# Revit family: Drain_Floor_7_Inch_Diameter_Top_Medium-Duty_Zurn-Z507
name_source: partatom
category: Plumbing Fixtures
units: mm (PartAtom-declared; Revit-internal decimal feet)

## family parameters
Always vertical = Yes
Cut with Voids When Loaded = No
Maintain Annotation Orientation = No
OmniClass Number = 23.70.50.21.24.14
OmniClass Title = Deck Waste Water Drains
Part Type = Normal
Room Calculation Point = No
Round Connector Dimension = Use Radius
Shared = No
Work Plane-Based = No

## types (20) — shared parameters
Default Elevation = 0' - 0"
Description = 7 Inch Diameter Top Medium-Duty Drain
Frame only height = 0' - 2 1/4"
Grate Radius = 0' - 3 3/16"
HW Connection = No
Main Material = Iron - Zurn - Cast - Painted - Blue
Manufacturer = Zurn Water, LLC
Manufacurer Brand = Zurn
Model = Z507
Product Documentation Link = https://files.zurn.com
Product Page URL = https://www.zurn.com
Product data url = https://bimobject.com
Trap Primer Radius = 0' - 0 1/4"
URL = www.zurn.com
Veneer Frame = Bronze - Zurn  - Polished Nickel
Vent Connection = No

## per-type parameters (varying)
| type | Approx. Weight (Lbs) | Assembly Code | CW Connection | E Body Height | Flange Height | Frame | Grate | Outlet Radius | Outllet Outer Radius | Type Comments |
| Z507-4IC Outlet | 27 |  | Yes | 0' - 3 3/4" | 0' - 1 15/16" | No | Iron - Zurn - Cast - Painted - Blue | 0' - 2" | 0' - 2 27/32" | Z507-4IC Outlet w/ Optional-P Trap Primer Connection |
| ZN507-4IC Outlet | 27 |  | No | 0' - 3 3/4" | 0' - 2 1/8" | Yes | Bronze - Zurn  - Polished Nickel | 0' - 2" | 0' - 2 27/32" | ZN507-4IC Outlet w/ Optional-P Trap Primer Connection |
| Z507-3IP Outlet | 27 |  | Yes | 0' - 2 3/4" | 0' - 1 15/16" | No | Iron - Zurn - Cast - Painted - Blue | 0' - 1 1/2" | 0' - 2 1/4" | Z507-3IP Outlet w/ Optional-P Trap Primer Connection |
| Z507-4IP Outlet | 27 |  | No | 0' - 2 3/4" | 0' - 1 15/16" | No | Iron - Zurn - Cast - Painted - Blue | 0' - 2" | 0' - 2 13/16" | Z507-4IP Outlet w/ Optional-P Trap Primer Connection |
| Z507-2NH Outlet | 27 | D2030300 | Yes | 0' - 4 3/4" | 0' - 1 15/16" | No | Iron - Zurn - Cast - Painted - Blue | 0' - 1" | 0' - 1 7/32" | Z507-2NH Outlet w/ Optional-P Trap Primer Connection |
| Z507-3NH Outlet | 27 |  | Yes | 0' - 4 3/4" | 0' - 1 15/16" | No | Iron - Zurn - Cast - Painted - Blue | 0' - 1 1/2" | 0' - 1 23/32" | Z507-3NH Outlet w/ Optional-P Trap Primer Connection |
| Z507-4NH Outlet | 27 |  | No | 0' - 4 3/4" | 0' - 1 15/16" | No | Iron - Zurn - Cast - Painted - Blue | 0' - 2" | 0' - 2 7/32" | Z507-4NH Outlet w/ Optional-P Trap Primer Connection |
| Z507-6NH Outlet | 29 |  | No | 0' - 5 1/4" | 0' - 1 15/16" | No | Iron - Zurn - Cast - Painted - Blue | 0' - 3" | 0' - 3 3/16" | Z507-6NH Outlet w/ Optional-P Trap Primer Connection |
| Z507-2NL Outlet | 27 |  | Yes | 0' - 3 9/16" | 0' - 1 15/16" | No | Iron - Zurn - Cast - Painted - Blue | 0' - 1" | 0' - 1 11/16" | Z507-2NL Outlet w/ Optional-P Trap Primer Connection |
| Z507-3NL Outlet | 27 |  | Yes | 0' - 3 9/16" | 0' - 1 15/16" | No | Iron - Zurn - Cast - Painted - Blue | 0' - 1 1/2" | 0' - 2 7/32" | Z507-3NL Outlet w/ Optional-P Trap Primer Connection |
| Z507-4NL Outlet | 27 |  | Yes | 0' - 3 9/16" | 0' - 1 15/16" | No | Iron - Zurn - Cast - Painted - Blue | 0' - 2" | 0' - 2 27/32" | Z507-3NL Outlet w/ Optional-P Trap Primer Connection |
| ZN507-3IP Outlet | 27 | D2030300 | Yes | 0' - 2 3/4" | 0' - 2 1/8" | Yes | Bronze - Zurn  - Polished Nickel | 0' - 1 1/2" | 0' - 2 1/4" | ZN507-3IP Outlet w/ Optional-P Trap Primer Connection |
| ZN507-4IP Outlet | 27 |  | No | 0' - 2 3/4" | 0' - 2 1/8" | Yes | Bronze - Zurn  - Polished Nickel | 0' - 2" | 0' - 2 13/16" | ZN507-4IP Outlet w/ Optional-P Trap Primer Connection |
| ZN507-2NH Outlet | 27 |  | No | 0' - 4 3/4" | 0' - 2 1/8" | Yes | Bronze - Zurn  - Polished Nickel | 0' - 1" | 0' - 1 7/32" | ZN507-2NH Outlet w/ Optional-P Trap Primer Connection |
| ZN507-3NH Outlet | 27 |  | No | 0' - 4 3/4" | 0' - 2 1/8" | Yes | Bronze - Zurn  - Polished Nickel | 0' - 1 1/2" | 0' - 1 23/32" | ZN507-3NH Outlet w/ Optional-P Trap Primer Connection |
| ZN507-4NH Outlet | 27 |  | No | 0' - 4 3/4" | 0' - 2 1/8" | Yes | Bronze - Zurn  - Polished Nickel | 0' - 2" | 0' - 2 7/32" | ZN507-4NH Outlet w/ Optional-P Trap Primer Connection |
| ZN507-6NH Outlet | 29 |  | No | 0' - 5 1/4" | 0' - 2 1/8" | Yes | Bronze - Zurn  - Polished Nickel | 0' - 3" | 0' - 3 3/16" | ZN507-6NH Outlet w/ Optional-P Trap Primer Connection |
| ZN507-2NL Outlet | 27 |  | Yes | 0' - 3 9/16" | 0' - 2 1/8" | Yes | Bronze - Zurn  - Polished Nickel | 0' - 1" | 0' - 1 11/16" | ZN507-2NL Outlet w/ Optional-P Trap Primer Connection |
| ZN507-3NL Outlet | 27 |  | No | 0' - 3 9/16" | 0' - 2 1/8" | Yes | Bronze - Zurn  - Polished Nickel | 0' - 1 1/2" | 0' - 2 7/32" | ZN507-3NL Outlet w/ Optional-P Trap Primer Connection |
| ZN507-4NL Outlet | 27 |  | No | 0' - 3 9/16" | 0' - 2 1/8" | Yes | Bronze - Zurn  - Polished Nickel | 0' - 2" | 0' - 2 27/32" | ZN507-4NL Outlet w/ Optional-P Trap Primer Connection |

## geometry (parser evidence)
native form markers: Sweep x4
no freeform markers — native parametric forms only
